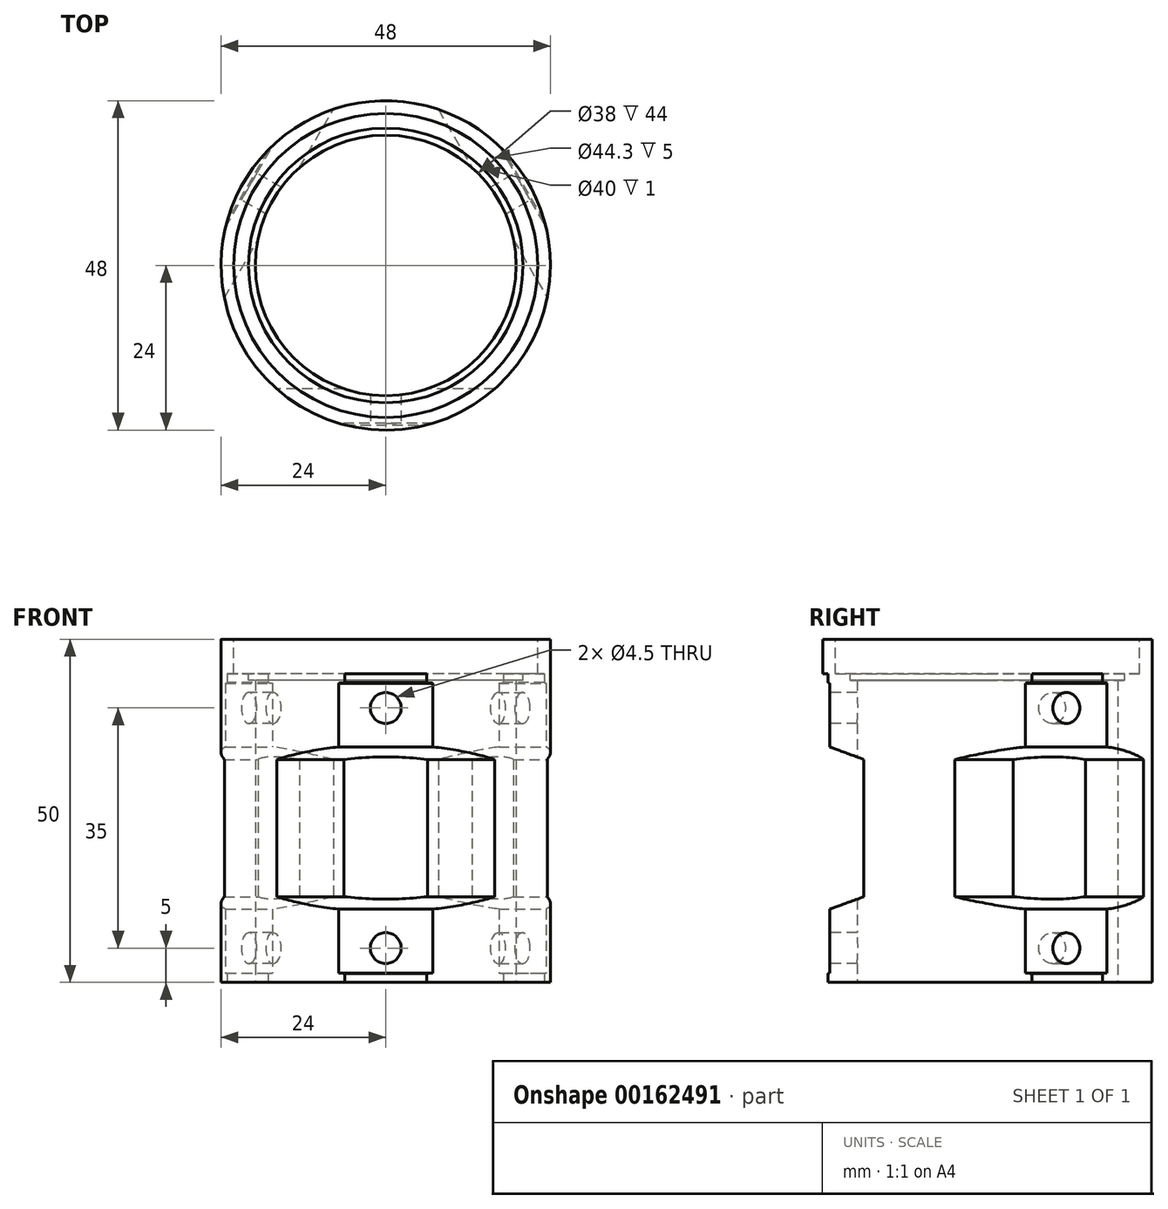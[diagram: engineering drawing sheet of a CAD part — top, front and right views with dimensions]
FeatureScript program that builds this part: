
annotation { "Feature Type Name" : "Feature", "Feature Type Description" : "" }
export const myFeature = defineFeature(function(context is Context, id is Id, definition is map)
    precondition{}
    {
        {
            var Q0;
            Q0=qCreatedBy(makeId("Top.planeOp"),FACE);
            var sketch = newSketch(context, id + "F0", { "sketchPlane" : qUnion([Q0])});
            skCircle(sketch, "E0", {"center": v(0, 0) * mm, "radius": 19 * mm});
            skCircle(sketch, "E1", {"center": v(0, 0) * mm, "radius": 24 * mm});
            skSolve(sketch);
        }
        {
            var Q0;
            Q0 = qSketchRegion(id + "F0", true);
            extrude(context, id + "F1", {"entities" : qUnion([Q0]), "depth" : 50 * mm});
        }
        {
            var Q0;
            Q0=makeQuery(id+"F1.opExtrude","CAP_FACE",FACE,{"disambiguationData":[OSD([sQuery(id+"F0.wireOp",EDGE,"E0"),sQuery(id+"F0.wireOp",EDGE,"E1")])],"isStart":false});
            var sketch = newSketch(context, id + "F2", { "sketchPlane" : qUnion([Q0])});
            skCircle(sketch, "E2", {"center": v(0, 0) * mm, "radius": 22.15 * mm});
            skSolve(sketch);
        }
        {
            var Q0;
            Q0 = qSketchRegion(id + "F2", true);
            extrude(context, id + "F3", {"entities" : qUnion([Q0]), "operationType" : NewBodyOperationType.REMOVE, "oppositeDirection" : true, "depth" : 5 * mm});
        }
        {
            var Q0;
            Q0=makeQuery(id+"F3.boolean.opBoolean","COPY",FACE,{"derivedFrom":makeQuery(id+"F3.opExtrude","CAP_FACE",FACE,{"disambiguationData":[OSD([sQuery(id+"F2.wireOp",EDGE,"E2")])],"isStart":false})});
            var sketch = newSketch(context, id + "F4", { "sketchPlane" : qUnion([Q0])});
            skCircle(sketch, "E3", {"center": v(0, 0) * mm, "radius": 20 * mm});
            skSolve(sketch);
        }
        {
            var Q0;
            Q0 = qSketchRegion(id + "F4", true);
            extrude(context, id + "F5", {"entities" : qUnion([Q0]), "operationType" : NewBodyOperationType.REMOVE, "oppositeDirection" : true, "depth" : 1 * mm});
        }
        {
            var Q0;
            Q0=qCreatedBy(makeId("Top.planeOp"),FACE);
            var sketch = newSketch(context, id + "F6", { "sketchPlane" : qUnion([Q0])});
            skCircle(sketch, "E4.cCircle", {"center": v(0, 0) * mm, "radius": 23.25 * mm, "construction": true});
            skLineSegment(sketch, "E4.0", {"start": v(40.27, -23.25) * mm, "end": v(-40.27, -23.25) * mm});
            skLineSegment(sketch, "E4.1", {"start": v(-40.27, -23.25) * mm, "end": v(0, 46.5) * mm});
            skLineSegment(sketch, "E4.2", {"start": v(0, 46.5) * mm, "end": v(40.27, -23.25) * mm});
            skPoint(sketch, "E4.0.midPoint", {"position": v(0, -23.25) * mm});
            skCircle(sketch, "E5", {"center": v(0, 0) * mm, "radius": 57.97 * mm});
            skSolve(sketch);
        }
        {
            var Q0;
            Q0 = qSketchRegion(id + "F6", true);
            extrude(context, id + "F7", {"entities" : qUnion([Q0]), "operationType" : NewBodyOperationType.REMOVE, "depth" : 45 * mm});
        }
        {
            var Q0;
            Q0=qCreatedBy(makeId("Right.planeOp"),FACE);
            var sketch = newSketch(context, id + "F8", { "sketchPlane" : qUnion([Q0])});
            skLineSegment(sketch, "E6", {"start": v(-23, 43.61) * mm, "end": v(-23, 34.32) * mm});
            skLineSegment(sketch, "E7", {"start": v(-23, 43.61) * mm, "end": v(-27.33, 45.2) * mm});
            skLineSegment(sketch, "E8", {"start": v(0, 22.5) * mm, "end": v(-27.9, 22.5) * mm, "construction": true});
            skLineSegment(sketch, "E9", {"start": v(-23, 34.32) * mm, "end": v(-18, 32.5) * mm});
            skLineSegment(sketch, "E10", {"start": v(-18, 32.5) * mm, "end": v(-18, 22.5) * mm});
            skLineSegment(sketch, "E11.trimOffspring", {"start": v(-23, 22.5) * mm, "end": v(-23, 0) * mm});
            skLineSegment(sketch, "E12.MirrorCS", {"start": v(-18, 12.5) * mm, "end": v(-18, 22.5) * mm});
            skLineSegment(sketch, "E13.MirrorCS", {"start": v(-23, 10.68) * mm, "end": v(-18, 12.5) * mm});
            skLineSegment(sketch, "E14.MirrorCS", {"start": v(-23, 1.39) * mm, "end": v(-23, 10.68) * mm});
            skLineSegment(sketch, "E15.MirrorCS", {"start": v(-23, 1.39) * mm, "end": v(-27.33, -0.2) * mm});
            skLineSegment(sketch, "E16", {"start": v(-27.33, 45.2) * mm, "end": v(-27.33, -0.2) * mm});
            skSolve(sketch);
        }
        {
            var Q0;
            Q0 = qSketchRegion(id + "F8", true);
            extrude(context, id + "F9", {"entities" : qUnion([Q0]), "endBound" : BoundingType.SYMMETRIC, "depth" : 50 * mm});
        }
        {
            var Q0;
            Q0=makeQuery(id+"F9.opExtrude","SWEPT_BODY",BODY,{"disambiguationData":[OSD([sQuery(id+"F8.wireOp",EDGE,"E6"),sQuery(id+"F8.wireOp",EDGE,"E7"),sQuery(id+"F8.wireOp",EDGE,"E9"),sQuery(id+"F8.wireOp",EDGE,"E10"),sQuery(id+"F8.wireOp",EDGE,"E12.MirrorCS"),sQuery(id+"F8.wireOp",EDGE,"E13.MirrorCS"),sQuery(id+"F8.wireOp",EDGE,"E14.MirrorCS"),sQuery(id+"F8.wireOp",EDGE,"E15.MirrorCS"),sQuery(id+"F8.wireOp",EDGE,"E16")])]});
            var Q1;
            Q1=makeQuery(id+"F1.opExtrude","SWEPT_FACE",FACE,{"disambiguationData":[OSD([sQuery(id+"F0.wireOp",EDGE,"E0")])]});
            circularPattern(context, id + "F10", {"entities" : qUnion([Q0]), "axis" : qUnion([Q1]), "angle" : 120 * degree, "instanceCount" : 3});
        }
        {
            var Q0;
            Q0=makeQuery(id+"F10.opPattern","COPY",BODY,{"derivedFrom":makeQuery(id+"F9.opExtrude","SWEPT_BODY",BODY,{"disambiguationData":[OSD([sQuery(id+"F8.wireOp",EDGE,"E6"),sQuery(id+"F8.wireOp",EDGE,"E7"),sQuery(id+"F8.wireOp",EDGE,"E9"),sQuery(id+"F8.wireOp",EDGE,"E10"),sQuery(id+"F8.wireOp",EDGE,"E12.MirrorCS"),sQuery(id+"F8.wireOp",EDGE,"E13.MirrorCS"),sQuery(id+"F8.wireOp",EDGE,"E14.MirrorCS"),sQuery(id+"F8.wireOp",EDGE,"E15.MirrorCS"),sQuery(id+"F8.wireOp",EDGE,"E16")])]}),"instanceName":"2"});
            var Q1;
            Q1=makeQuery(id+"F10.opPattern","COPY",BODY,{"derivedFrom":makeQuery(id+"F9.opExtrude","SWEPT_BODY",BODY,{"disambiguationData":[OSD([sQuery(id+"F8.wireOp",EDGE,"E6"),sQuery(id+"F8.wireOp",EDGE,"E7"),sQuery(id+"F8.wireOp",EDGE,"E9"),sQuery(id+"F8.wireOp",EDGE,"E10"),sQuery(id+"F8.wireOp",EDGE,"E12.MirrorCS"),sQuery(id+"F8.wireOp",EDGE,"E13.MirrorCS"),sQuery(id+"F8.wireOp",EDGE,"E14.MirrorCS"),sQuery(id+"F8.wireOp",EDGE,"E15.MirrorCS"),sQuery(id+"F8.wireOp",EDGE,"E16")])]}),"instanceName":"1"});
            var Q2;
            Q2=makeQuery(id+"F9.opExtrude","SWEPT_BODY",BODY,{"disambiguationData":[OSD([sQuery(id+"F8.wireOp",EDGE,"E6"),sQuery(id+"F8.wireOp",EDGE,"E7"),sQuery(id+"F8.wireOp",EDGE,"E9"),sQuery(id+"F8.wireOp",EDGE,"E10"),sQuery(id+"F8.wireOp",EDGE,"E12.MirrorCS"),sQuery(id+"F8.wireOp",EDGE,"E13.MirrorCS"),sQuery(id+"F8.wireOp",EDGE,"E14.MirrorCS"),sQuery(id+"F8.wireOp",EDGE,"E15.MirrorCS"),sQuery(id+"F8.wireOp",EDGE,"E16")])]});
            var Q3;
            Q3=makeQuery(id+"F1.opExtrude","SWEPT_BODY",BODY,{"disambiguationData":[OSD([sQuery(id+"F0.wireOp",EDGE,"E0"),sQuery(id+"F0.wireOp",EDGE,"E1")])]});
            booleanBodies(context, id + "F11", {"operationType" : BooleanOperationType.SUBTRACTION, "tools" : qUnion([Q0, Q1, Q2]), "targets" : qUnion([Q3])});
        }
        {
            var Q0;
            Q0=makeQuery(id+"F11.opBoolean","COPY",FACE,{"derivedFrom":makeQuery(id+"F9.opExtrude","SWEPT_FACE",FACE,{"disambiguationData":[OSD([sQuery(id+"F8.wireOp",EDGE,"E6")])]})});
            var sketch = newSketch(context, id + "F12", { "sketchPlane" : qUnion([Q0])});
            skCircle(sketch, "E17", {"center": v(0, 40) * mm, "radius": 2.25 * mm});
            skCircle(sketch, "E18", {"center": v(0, 5) * mm, "radius": 2.25 * mm});
            skSolve(sketch);
        }
        {
            var Q0;
            Q0 = qSketchRegion(id + "F12", true);
            extrude(context, id + "F13", {"entities" : qUnion([Q0]), "oppositeDirection" : true, "depth" : 10 * mm, "hasSecondDirection" : true, "secondDirectionOppositeDirection" : false, "secondDirectionDepth" : 10 * mm});
        }
        {
            var Q0;
            Q0=makeQuery(id+"F13.opExtrude","SWEPT_BODY",BODY,{"disambiguationData":[OSD([sQuery(id+"F12.wireOp",EDGE,"E17")])]});
            var Q1;
            Q1=makeQuery(id+"F13.opExtrude","SWEPT_BODY",BODY,{"disambiguationData":[OSD([sQuery(id+"F12.wireOp",EDGE,"E18")])]});
            var Q2;
            Q2=makeQuery(id+"F1.opExtrude","SWEPT_FACE",FACE,{"disambiguationData":[OSD([sQuery(id+"F0.wireOp",EDGE,"E0")])]});
            circularPattern(context, id + "F14", {"entities" : qUnion([Q0, Q1]), "axis" : qUnion([Q2]), "angle" : 120 * degree, "instanceCount" : 3});
        }
        {
            var Q0;
            Q0=makeQuery(id+"F14.opPattern","COPY",BODY,{"derivedFrom":makeQuery(id+"F13.opExtrude","SWEPT_BODY",BODY,{"disambiguationData":[OSD([sQuery(id+"F12.wireOp",EDGE,"E17")])]}),"instanceName":"2"});
            var Q1;
            Q1=makeQuery(id+"F14.opPattern","COPY",BODY,{"derivedFrom":makeQuery(id+"F13.opExtrude","SWEPT_BODY",BODY,{"disambiguationData":[OSD([sQuery(id+"F12.wireOp",EDGE,"E18")])]}),"instanceName":"2"});
            var Q2;
            Q2=makeQuery(id+"F14.opPattern","COPY",BODY,{"derivedFrom":makeQuery(id+"F13.opExtrude","SWEPT_BODY",BODY,{"disambiguationData":[OSD([sQuery(id+"F12.wireOp",EDGE,"E17")])]}),"instanceName":"1"});
            var Q3;
            Q3=makeQuery(id+"F14.opPattern","COPY",BODY,{"derivedFrom":makeQuery(id+"F13.opExtrude","SWEPT_BODY",BODY,{"disambiguationData":[OSD([sQuery(id+"F12.wireOp",EDGE,"E18")])]}),"instanceName":"1"});
            var Q4;
            Q4=makeQuery(id+"F13.opExtrude","SWEPT_BODY",BODY,{"disambiguationData":[OSD([sQuery(id+"F12.wireOp",EDGE,"E17")])]});
            var Q5;
            Q5=makeQuery(id+"F13.opExtrude","SWEPT_BODY",BODY,{"disambiguationData":[OSD([sQuery(id+"F12.wireOp",EDGE,"E18")])]});
            var Q6;
            Q6=makeQuery(id+"F1.opExtrude","SWEPT_BODY",BODY,{"disambiguationData":[OSD([sQuery(id+"F0.wireOp",EDGE,"E0"),sQuery(id+"F0.wireOp",EDGE,"E1")])]});
            booleanBodies(context, id + "F15", {"operationType" : BooleanOperationType.SUBTRACTION, "tools" : qUnion([Q0, Q1, Q2, Q3, Q4, Q5]), "targets" : qUnion([Q6])});
        }
    });
